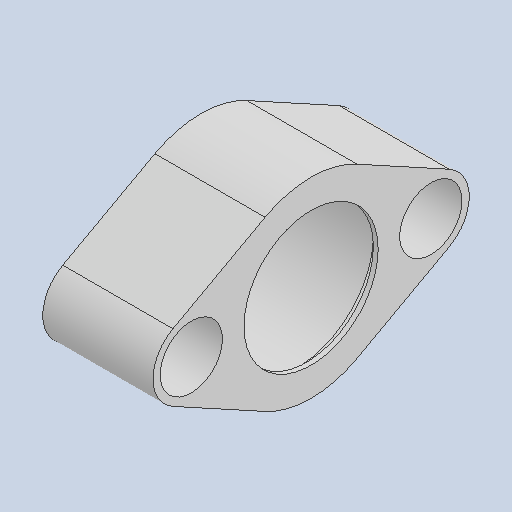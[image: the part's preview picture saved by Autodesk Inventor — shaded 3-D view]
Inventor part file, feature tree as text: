
AUTODESK INVENTOR PART (.ipt)
format: ipt  version: 2022 (Build 260153000, 153)  size: 156,672 bytes
history: native  units: in
note: dims shown in document units (in); Inventor stores cm internally (conversion verified against a paired STEP export)
features: sketch x5, hole x2, chamfer x2, plane x1, extrude x1
ambient origin geometry x8: Origin, YZ Plane, XZ Plane, XY Plane, X Axis, Y Axis, Z Axis, Center Point
bodies: Body1 (feature_tree)
feature tree (11):
  plane  "Work Plane1"
  extrude  "Extrusion1"  Depth=0.4528in TaperAngle=0.0deg
  hole  "Hole2"  [1 undecoded]
  hole  "Hole1"  [1 undecoded]
  chamfer  "Chamfer2"  Distance=0.0197in
  chamfer  "Chamfer1"  Distance=0.0394in
  sketch  "Sketch1"  dims[d0=-0.3937in d1=0.4528in d2=0.0in]
  sketch  "Sketch2"  dims[d3=0.5512in d4=0.2362in d5=0.1575in d6=0.0787in d7=90.0deg d8=0.315in d9=0.8108in]
  sketch  "Sketch3"  dims[d10=0.126in d11=0.2362in d12=0.2559in d13=0.2362in d14=90.0deg d15=0.315in d16=0.0in]
  sketch  "Sketch4"  dims[d17=0.126in d18=0.2362in d19=0.2559in d20=0.2362in d21=90.0deg d22=0.315in d23=0.0in]
  sketch  "Sketch5"  dims[d24=0.6299in d25=0.2362in d26=0.1575in d27=0.0787in d28=90.0deg d29=0.3937in d30=0.6184in d31=0.0197in d32=0.0197in d33=17.7165in d34=0.0197in d35=0.0197in d36=17.7165in d37=0.0197in d38=0.0197in d39=17.7165in d40=0.0394in d41=0.0394in d42=0.0394in d43=0.0059in d44=0.0098in d45=0.0148in d46=32.2835in d47=0.0295in d48=46.4567in d49=0.0025in d50=0.0295in d51=0.0148in]
note: 2 required parameter values undecoded (feature->parameter linkage not recoverable at this tier; creation-order binding heuristic only, values carry confidence <= 0.55)
